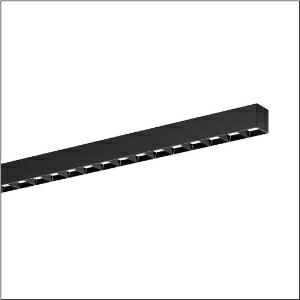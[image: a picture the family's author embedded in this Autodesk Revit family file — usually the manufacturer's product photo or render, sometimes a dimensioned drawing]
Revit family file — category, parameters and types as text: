
# Revit family: silica_r__21_51mx21tctab_539a
name_source: partatom
category: Lighting Fixtures
units: mm (PartAtom-declared; Revit-internal decimal feet)

## family parameters
Cut with Voids When Loaded = No
Host = Face
Light Source = No
Part Type = Normal
Room Calculation Point = No
Round Connector Dimension = Use Diameter
Shared = No

## types (1)
- --- (1 x LED, 9300 lm, 80.5 W, 6500K)
    Apparent Load = 81 VA
    CIE Flux Codes = 85 99 100 100 100
    Color Rendering = 80
    Color Temperature = 6500K
    Default Elevation = 1800 mm
    Description = Silica® 21, office luminaire, primary light control with darklight reflector, of PMMA, black, CAT 2 (L<= 3000cd/m²), light emission: direct distribution, primary light characteristic: symmetric, installation type: surface-mounted, LED, rated luminous flux: 9.300lm, luminous efficacy: 110lm/W, light colour: 8tw, colour temperature: 2700..6500K, control gear: ECG DALI, with terminal, 3+2-pole, max. 2.5mm², mains connection: 220..240V, AC, 50/60Hz, rated input power: 84.6W, luminaire housing, of aluminium, jet black (RAL 9005), length: 3.004mm, width: 53mm, height: 53mm, protection rating (complete): IP20, insulation class (complete): insulation class I (protective earthing), certification: CE, permissible operating ambient temperature: 0..+35°C, standard: EN 50419, packaging unit: 1 piece
    Height = 0 mm  [stored 0 ft]
    Lamp = 1 x LED
    Lamp Light Flux = 9300 lm
    Lamp Power = 80.5 W
    Lamp count = 1
    Length = 3004 mm
    Luminous efficacy = 116 lm/W
    Manufacturer = Siteco
    ModVariant = No
    Model = 51MX21TCTAB
    Mounting Place = Ceiling
    Mounting Type = Recessed
    Number of Poles = 1
    OnlyDefault = Yes
    Power Factor = 1
    Product Name = Silica® 21
    Product group = office luminaire | ceiling recessed
    ProductGroupID = 401
    Protection Class = Protection class I
    Protection Degree = IP 20
    RLX_Detail_Level = 1
    RLX_Emergency_Light_Flux = 0 lm
    RLX_Emergency_Type = 0
    RLX_Emergency_Type_DB = No
    RlxData = <blob elided: 60809 chars, md5=31cdc30a>
    Socket = socket
    Standby Power = 0 W
    System Light Flux = 9300 lm
    System Power = 81 W
    Type Comments = individual setting
    Type Image = l_1297756.jpg
    URL = http://relux.com
    VarID = @adj_071383
    Voltage = 0 V
    Weight = 0.00 kg
    Width = 53 mm

note: [stored X ft] marks values corroborated as IEEE doubles in the binary element streams (Revit-internal decimal feet)

## geometry (parser evidence)
native form markers: Blend x4, Sweep x11
no freeform markers — native parametric forms only
